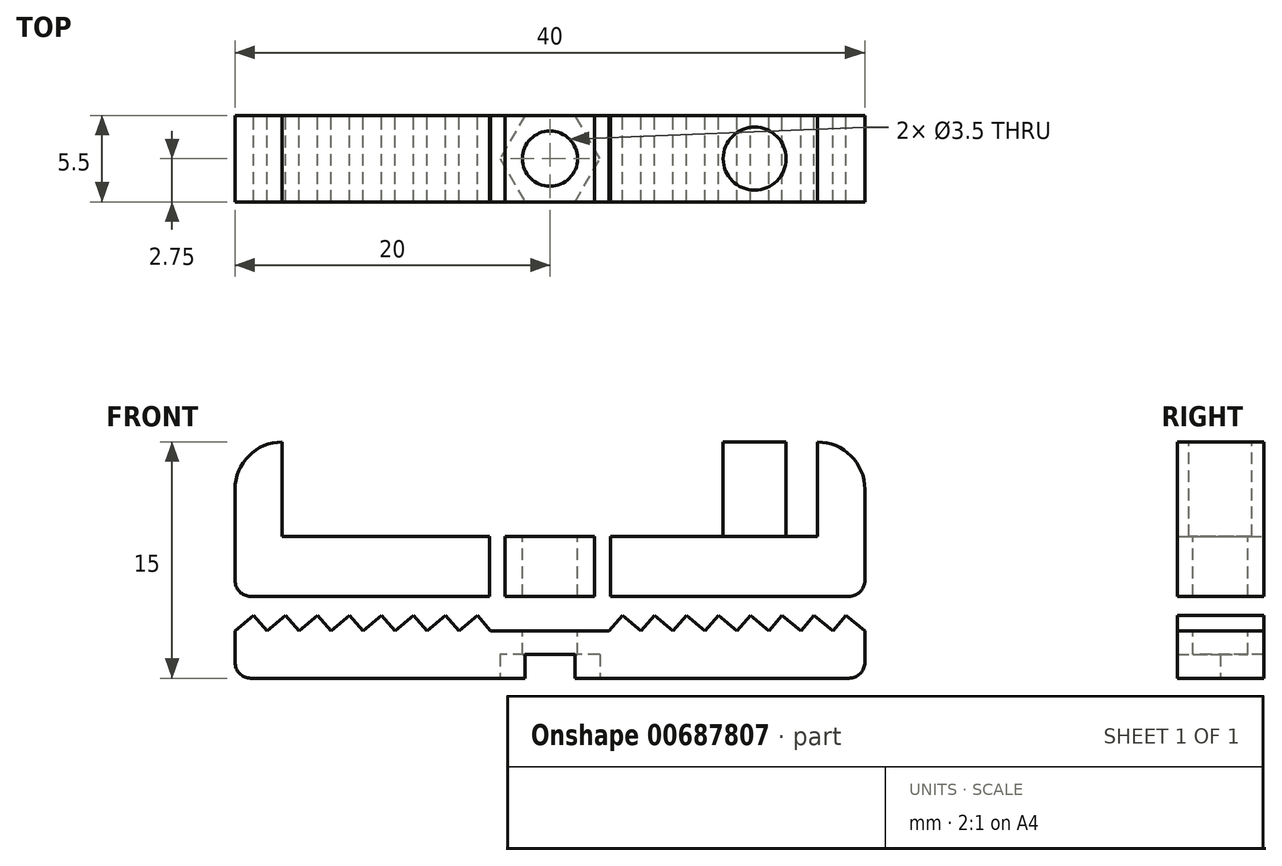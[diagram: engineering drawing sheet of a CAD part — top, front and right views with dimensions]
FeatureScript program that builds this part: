
annotation { "Feature Type Name" : "Feature", "Feature Type Description" : "" }
export const myFeature = defineFeature(function(context is Context, id is Id, definition is map)
    precondition{}
    {
        {
            var Q0;
            Q0=qCreatedBy(makeId("Top.planeOp"),FACE);
            var sketch = newSketch(context, id + "F0", { "sketchPlane" : qUnion([Q0])});
            skLineSegment(sketch, "E0.bottom", {"start": v(-20, 2.75) * mm, "end": v(20, 2.75) * mm});
            skLineSegment(sketch, "E0.top", {"start": v(-20, -2.75) * mm, "end": v(20, -2.75) * mm});
            skLineSegment(sketch, "E0.left", {"start": v(-20, 2.75) * mm, "end": v(-20, -2.75) * mm});
            skLineSegment(sketch, "E0.right", {"start": v(20, 2.75) * mm, "end": v(20, -2.75) * mm});
            skSolve(sketch);
        }
        {
            var Q0;
            Q0=makeQuery(id+"F0.imprint","IMPRINT",FACE,{"disambiguationData":[TD([[makeQuery(id+"F0.imprint","IMPRINT",EDGE,{"derivedFrom":sQuery(id+"F0.wireOp",EDGE,"E0.bottom")}),-1.0]])]});
            extrude(context, id + "F1", {"entities" : qUnion([Q0]), "depth" : 15 * mm, "offsetDistance" : 25 * mm});
        }
        {
            var Q0;
            Q0=makeQuery(id+"F1.opExtrude","SWEPT_FACE",FACE,{"disambiguationData":[OSD([sQuery(id+"F0.wireOp",EDGE,"E0.bottom")])]});
            var sketch = newSketch(context, id + "F2", { "sketchPlane" : qUnion([Q0])});
            skLineSegment(sketch, "E1.bottom", {"start": v(3.76, 3) * mm, "end": v(0, 3) * mm});
            skLineSegment(sketch, "E1.top", {"start": v(20, 5.2) * mm, "end": v(3.84, 5.2) * mm});
            skLineSegment(sketch, "E1.left", {"start": v(20, 3) * mm, "end": v(20, 5.2) * mm});
            skLineSegment(sketch, "E2.MirrorCS", {"start": v(-20, 5.2) * mm, "end": v(-3.84, 5.2) * mm});
            skLineSegment(sketch, "E3.MirrorCS", {"start": v(-20, 3) * mm, "end": v(-20, 5.2) * mm});
            skLineSegment(sketch, "E4.top", {"start": v(2.84, 12.2) * mm, "end": v(3.84, 12.2) * mm});
            skLineSegment(sketch, "E4.left", {"start": v(2.84, 5.2) * mm, "end": v(2.84, 12.2) * mm});
            skLineSegment(sketch, "E4.right", {"start": v(3.84, 5.2) * mm, "end": v(3.84, 12.2) * mm});
            skLineSegment(sketch, "E5.MirrorCS", {"start": v(-2.84, 5.2) * mm, "end": v(-2.84, 12.2) * mm});
            skLineSegment(sketch, "E6.MirrorCS", {"start": v(-2.84, 12.2) * mm, "end": v(-3.84, 12.2) * mm});
            skLineSegment(sketch, "E7.MirrorCS", {"start": v(-3.84, 5.2) * mm, "end": v(-3.84, 12.2) * mm});
            skLineSegment(sketch, "E8.trimOffspring", {"start": v(-2.84, 5.2) * mm, "end": v(0, 5.2) * mm});
            skLineSegment(sketch, "E9.trimOffspring", {"start": v(2.84, 5.2) * mm, "end": v(0, 5.2) * mm});
            skLineSegment(sketch, "E10", {"start": v(20, 4) * mm, "end": v(3.88, 4) * mm, "construction": true});
            skLineSegment(sketch, "E11", {"start": v(20, 3) * mm, "end": v(18.81, 4) * mm});
            skLineSegment(sketch, "E12", {"start": v(18.81, 4) * mm, "end": v(17.97, 3) * mm});
            skLineSegment(sketch, "E13", {"start": v(17.97, 3) * mm, "end": v(16.78, 4) * mm});
            skLineSegment(sketch, "E14", {"start": v(16.78, 4) * mm, "end": v(15.94, 3) * mm});
            skLineSegment(sketch, "E15", {"start": v(15.94, 3) * mm, "end": v(14.75, 4) * mm});
            skLineSegment(sketch, "E16", {"start": v(14.75, 4) * mm, "end": v(13.9, 3) * mm});
            skLineSegment(sketch, "E17", {"start": v(13.9, 3) * mm, "end": v(12.72, 4) * mm});
            skLineSegment(sketch, "E18", {"start": v(12.72, 4) * mm, "end": v(11.88, 3) * mm});
            skLineSegment(sketch, "E19", {"start": v(11.88, 3) * mm, "end": v(10.7, 4) * mm});
            skLineSegment(sketch, "E20", {"start": v(10.7, 4) * mm, "end": v(9.85, 3) * mm});
            skLineSegment(sketch, "E21", {"start": v(9.85, 3) * mm, "end": v(8.66, 4) * mm});
            skLineSegment(sketch, "E22", {"start": v(8.66, 4) * mm, "end": v(7.82, 3) * mm});
            skLineSegment(sketch, "E23", {"start": v(7.82, 3) * mm, "end": v(6.63, 4) * mm});
            skLineSegment(sketch, "E24", {"start": v(6.63, 4) * mm, "end": v(5.79, 3) * mm});
            skLineSegment(sketch, "E25", {"start": v(5.79, 3) * mm, "end": v(4.6, 4) * mm});
            skLineSegment(sketch, "E26", {"start": v(4.6, 4) * mm, "end": v(3.76, 3) * mm});
            skLineSegment(sketch, "E27.MirrorCS", {"start": v(-4.6, 4) * mm, "end": v(-3.76, 3) * mm});
            skLineSegment(sketch, "E28.MirrorCS", {"start": v(-5.79, 3) * mm, "end": v(-4.6, 4) * mm});
            skLineSegment(sketch, "E29.MirrorCS", {"start": v(-6.63, 4) * mm, "end": v(-5.79, 3) * mm});
            skLineSegment(sketch, "E30.MirrorCS", {"start": v(-7.82, 3) * mm, "end": v(-6.63, 4) * mm});
            skLineSegment(sketch, "E31.MirrorCS", {"start": v(-8.66, 4) * mm, "end": v(-7.82, 3) * mm});
            skLineSegment(sketch, "E32.MirrorCS", {"start": v(-9.85, 3) * mm, "end": v(-8.66, 4) * mm});
            skLineSegment(sketch, "E33.MirrorCS", {"start": v(-10.7, 4) * mm, "end": v(-9.85, 3) * mm});
            skLineSegment(sketch, "E34.MirrorCS", {"start": v(-11.88, 3) * mm, "end": v(-10.7, 4) * mm});
            skLineSegment(sketch, "E35.MirrorCS", {"start": v(-12.72, 4) * mm, "end": v(-11.88, 3) * mm});
            skLineSegment(sketch, "E36.MirrorCS", {"start": v(-13.9, 3) * mm, "end": v(-12.72, 4) * mm});
            skLineSegment(sketch, "E37.MirrorCS", {"start": v(-14.75, 4) * mm, "end": v(-13.9, 3) * mm});
            skLineSegment(sketch, "E38.MirrorCS", {"start": v(-15.94, 3) * mm, "end": v(-14.75, 4) * mm});
            skLineSegment(sketch, "E39.MirrorCS", {"start": v(-16.78, 4) * mm, "end": v(-15.94, 3) * mm});
            skLineSegment(sketch, "E40.MirrorCS", {"start": v(-17.97, 3) * mm, "end": v(-16.78, 4) * mm});
            skLineSegment(sketch, "E41.MirrorCS", {"start": v(-18.81, 4) * mm, "end": v(-17.97, 3) * mm});
            skLineSegment(sketch, "E42.MirrorCS", {"start": v(-20, 3) * mm, "end": v(-18.81, 4) * mm});
            skLineSegment(sketch, "E43.trimOffspring", {"start": v(-3.76, 3) * mm, "end": v(0, 3) * mm});
            skPoint(sketch, "E44.MirrorCS.start.orphan", {"position": v(-20, 3) * mm});
            skSolve(sketch);
        }
        {
            var Q0;
            Q0=makeQuery(id+"F2.imprint","IMPRINT",FACE,{"disambiguationData":[TD([[makeQuery(id+"F2.imprint","IMPRINT",EDGE,{"derivedFrom":sQuery(id+"F2.wireOp",EDGE,"E1.bottom")}),-1.0]])]});
            var Q1;
            Q1=makeQuery(id+"F2.imprint","IMPRINT",FACE,{"disambiguationData":[TD([[makeQuery(id+"F2.imprint","IMPRINT",EDGE,{"derivedFrom":sQuery(id+"F2.wireOp",EDGE,"E44.MirrorCS")}),1.0]])]});
            extrude(context, id + "F3", {"entities" : qUnion([Q0, Q1]), "operationType" : NewBodyOperationType.REMOVE, "oppositeDirection" : true, "depth" : 6 * mm, "offsetDistance" : 25 * mm});
        }
        {
            var Q0;
            Q0=makeQuery(id+"F1.opExtrude","CAP_EDGE",EDGE,{"disambiguationData":[OSD([sQuery(id+"F0.wireOp",EDGE,"E0.left")])],"isStart":false});
            var Q1;
            Q1=makeQuery(id+"F1.opExtrude","CAP_EDGE",EDGE,{"disambiguationData":[OSD([sQuery(id+"F0.wireOp",EDGE,"E0.right")])],"isStart":false});
            fillet(context, id + "F4", {"entities" : qUnion([Q0, Q1]), "radius" : 3 * mm, "tangentPropagation" : true, "allowEdgeOverflow" : false});
        }
        {
            var Q0;
            Q0=makeQuery(id+"F1.opExtrude","CAP_FACE",FACE,{"disambiguationData":[OSD([sQuery(id+"F0.wireOp",EDGE,"E0.bottom"),sQuery(id+"F0.wireOp",EDGE,"E0.top"),sQuery(id+"F0.wireOp",EDGE,"E0.left"),sQuery(id+"F0.wireOp",EDGE,"E0.right")])],"isStart":false});
            var sketch = newSketch(context, id + "F5", { "sketchPlane" : qUnion([Q0])});
            skCircle(sketch, "E45", {"center": v(-13, 0) * mm, "radius": 2 * mm});
            skCircle(sketch, "E46.MirrorC", {"center": v(13, 0) * mm, "radius": 2 * mm});
            skSolve(sketch);
        }
        {
            var Q0;
            Q0=makeQuery(id+"F5.imprint","IMPRINT",FACE,{"disambiguationData":[TD([[makeQuery(id+"F5.imprint","IMPRINT",EDGE,{"derivedFrom":sQuery(id+"F5.wireOp",EDGE,"E45")}),1.0]])]});
            var Q1;
            Q1=makeQuery(id+"F5.imprint","IMPRINT",FACE,{"disambiguationData":[TD([[makeQuery(id+"F5.imprint","IMPRINT",EDGE,{"derivedFrom":sQuery(id+"F5.wireOp",EDGE,"E46.MirrorC")}),-1.0]])]});
            extrude(context, id + "F6", {"entities" : qUnion([Q0, Q1]), "operationType" : NewBodyOperationType.REMOVE, "oppositeDirection" : true, "depth" : 6 * mm, "offsetDistance" : 25 * mm});
        }
        {
            var Q0;
            Q0=makeQuery(id+"F3.boolean.opBoolean","COPY",EDGE,{"derivedFrom":makeQuery(id+"F3.opExtrude","SWEPT_EDGE",EDGE,{"disambiguationData":[OSD([sQuery(id+"F0.wireOp",EDGE,"E0.bottom"),sQuery(id+"F0.wireOp",EDGE,"E0.left"),sQuery(id+"F2.wireOp",EDGE,"E1.top"),sQuery(id+"F2.wireOp",EDGE,"E1.left")])]})});
            var Q1;
            Q1=makeQuery(id+"F3.boolean.opBoolean","COPY",EDGE,{"derivedFrom":makeQuery(id+"F3.opExtrude","SWEPT_EDGE",EDGE,{"disambiguationData":[OSD([sQuery(id+"F0.wireOp",EDGE,"E0.bottom"),sQuery(id+"F0.wireOp",EDGE,"E0.left"),sQuery(id+"F2.wireOp",EDGE,"E1.bottom"),sQuery(id+"F2.wireOp",EDGE,"E1.left")])]})});
            var Q2;
            Q2=makeQuery(id+"F1.opExtrude","CAP_EDGE",EDGE,{"disambiguationData":[OSD([sQuery(id+"F0.wireOp",EDGE,"E0.left")])],"isStart":true});
            var Q3;
            Q3=makeQuery(id+"F1.opExtrude","CAP_EDGE",EDGE,{"disambiguationData":[OSD([sQuery(id+"F0.wireOp",EDGE,"E0.right")])],"isStart":true});
            var Q4;
            Q4=makeQuery(id+"F3.boolean.opBoolean","COPY",EDGE,{"derivedFrom":makeQuery(id+"F3.opExtrude","SWEPT_EDGE",EDGE,{"disambiguationData":[OSD([sQuery(id+"F0.wireOp",EDGE,"E0.bottom"),sQuery(id+"F0.wireOp",EDGE,"E0.right"),sQuery(id+"F2.wireOp",EDGE,"E44.MirrorCS"),sQuery(id+"F2.wireOp",EDGE,"E3.MirrorCS")])]})});
            var Q5;
            Q5=makeQuery(id+"F3.boolean.opBoolean","COPY",EDGE,{"derivedFrom":makeQuery(id+"F3.opExtrude","SWEPT_EDGE",EDGE,{"disambiguationData":[OSD([sQuery(id+"F0.wireOp",EDGE,"E0.bottom"),sQuery(id+"F0.wireOp",EDGE,"E0.right"),sQuery(id+"F2.wireOp",EDGE,"E2.MirrorCS"),sQuery(id+"F2.wireOp",EDGE,"E3.MirrorCS")])]})});
            fillet(context, id + "F7", {"entities" : qUnion([Q0, Q1, Q2, Q3, Q4, Q5]), "radius" : 1 * mm, "tangentPropagation" : true, "allowEdgeOverflow" : false});
        }
        {
            var Q0;
            Q0=makeQuery(id+"F1.opExtrude","CAP_FACE",FACE,{"disambiguationData":[OSD([sQuery(id+"F0.wireOp",EDGE,"E0.bottom"),sQuery(id+"F0.wireOp",EDGE,"E0.top"),sQuery(id+"F0.wireOp",EDGE,"E0.left"),sQuery(id+"F0.wireOp",EDGE,"E0.right")])],"isStart":true});
            var sketch = newSketch(context, id + "F8", { "sketchPlane" : qUnion([Q0])});
            skCircle(sketch, "E47.cCircle", {"center": v(0, 0) * mm, "radius": 2.75 * mm, "construction": true});
            skLineSegment(sketch, "E47.0", {"start": v(1.59, -2.75) * mm, "end": v(-1.59, -2.75) * mm});
            skLineSegment(sketch, "E47.1", {"start": v(-1.59, -2.75) * mm, "end": v(-3.18, 0) * mm});
            skLineSegment(sketch, "E47.2", {"start": v(-3.18, 0) * mm, "end": v(-1.59, 2.75) * mm});
            skLineSegment(sketch, "E47.3", {"start": v(-1.59, 2.75) * mm, "end": v(1.59, 2.75) * mm});
            skLineSegment(sketch, "E47.4", {"start": v(1.59, 2.75) * mm, "end": v(3.18, 0) * mm});
            skLineSegment(sketch, "E47.5", {"start": v(3.18, 0) * mm, "end": v(1.59, -2.75) * mm});
            skPoint(sketch, "E47.0.midPoint", {"position": v(0, -2.75) * mm});
            skSolve(sketch);
        }
        {
            var Q0;
            Q0=makeQuery(id+"F8.imprint","IMPRINT",FACE,{"disambiguationData":[TD([[makeQuery(id+"F8.imprint","IMPRINT",EDGE,{"derivedFrom":sQuery(id+"F8.wireOp",EDGE,"E47.0")}),1.0]])]});
            extrude(context, id + "F9", {"entities" : qUnion([Q0]), "operationType" : NewBodyOperationType.REMOVE, "oppositeDirection" : true, "depth" : 1.5 * mm, "offsetDistance" : 25 * mm});
        }
        {
            var Q0;
            Q0=makeQuery(id+"F1.opExtrude","CAP_FACE",FACE,{"disambiguationData":[OSD([sQuery(id+"F0.wireOp",EDGE,"E0.bottom"),sQuery(id+"F0.wireOp",EDGE,"E0.top"),sQuery(id+"F0.wireOp",EDGE,"E0.left"),sQuery(id+"F0.wireOp",EDGE,"E0.right")])],"isStart":false});
            var sketch = newSketch(context, id + "F10", { "sketchPlane" : qUnion([Q0])});
            skCircle(sketch, "E48", {"center": v(0, 0) * mm, "radius": 1.75 * mm});
            skSolve(sketch);
        }
        {
            var Q0;
            Q0=makeQuery(id+"F10.imprint","IMPRINT",FACE,{"disambiguationData":[TD([[makeQuery(id+"F10.imprint","IMPRINT",EDGE,{"derivedFrom":sQuery(id+"F10.wireOp",EDGE,"E48")}),1.0]])]});
            extrude(context, id + "F11", {"entities" : qUnion([Q0]), "operationType" : NewBodyOperationType.REMOVE, "oppositeDirection" : true, "depth" : 25 * mm, "offsetDistance" : 25 * mm});
        }
    });
